# Revit family: RL-1-E Return Valve Straight Model 3723
name_source: partatom
category: Rohrzubehör
revit_build: Autodesk Revit 2018 (Build: 20190510_1515(x64)
units: mm (PartAtom-declared; Revit-internal decimal feet)

## family parameters
Arbeitsebenenbasiert = Nein
Beim Laden mit Abzugskörper schneiden = Nein
Bemaßung runder Anschluss = Durchmesser verwenden
Gemeinsam genutzt = Nein
Immer vertikal = Nein
OmniClass-Nummer = 23.65.55.14
OmniClass-Titel = Valves for Liquid Services
Teiletyp = Unterbricht

## types (1)
- RL-1-E Return Valve Straight Model 3723
    Application = Water Heating Systems
Installation of the return valve permits shutting off the return connection of the radiator.
When the intake valve is shut at the same time, the radiator can be removed while the system is under pressure.
    Body = nickel-plated
    H03 = 15.5 mm  [stored 0.050853 ft]
    H05 = 17 mm  [stored 0.0557743 ft]
    H07 = 14 mm  [stored 0.0459318 ft]
    H6 = 8 mm  [stored 0.0262467 ft]
    Hersteller = HERZ Armaturen Ges.m.b.H.
    LO1 = 3 mm  [stored 0.00984252 ft]
    LO2 = 19.5 mm  [stored 0.0639764 ft]
    Max. operating pressure = 1000000.0 Pa
    Max. operating temperature = 110 °C
    Medium = Hot water purity according to ÖNORM H 5195 and/or VDI guideline 2035
    Model = Standard models with nickel-plated threaded sockets.
    R01 = 18 mm  [stored 0.0590551 ft]
    R02 = 19.5 mm  [stored 0.0639764 ft]
    R03 = 16.5 mm  [stored 0.0541339 ft]
    R04 = 17.5 mm  [stored 0.0574147 ft]
    R05 = 11.75 mm  [stored 0.0385499 ft]
    R06 = 10 mm  [stored 0.0328084 ft]
    S01 = 10 mm  [stored 0.0328084 ft]
    S03 = 61 mm  [stored 0.200131 ft]
    S04 = 45 mm  [stored 0.147638 ft]
    SCRNCODE = 05;01;02
    SCRNSEQ = ARM;ARM_TYP="ALLF";2
    URL = www.herzvalves.com

note: [stored X ft] marks values corroborated as IEEE doubles in the binary element streams (Revit-internal decimal feet)
